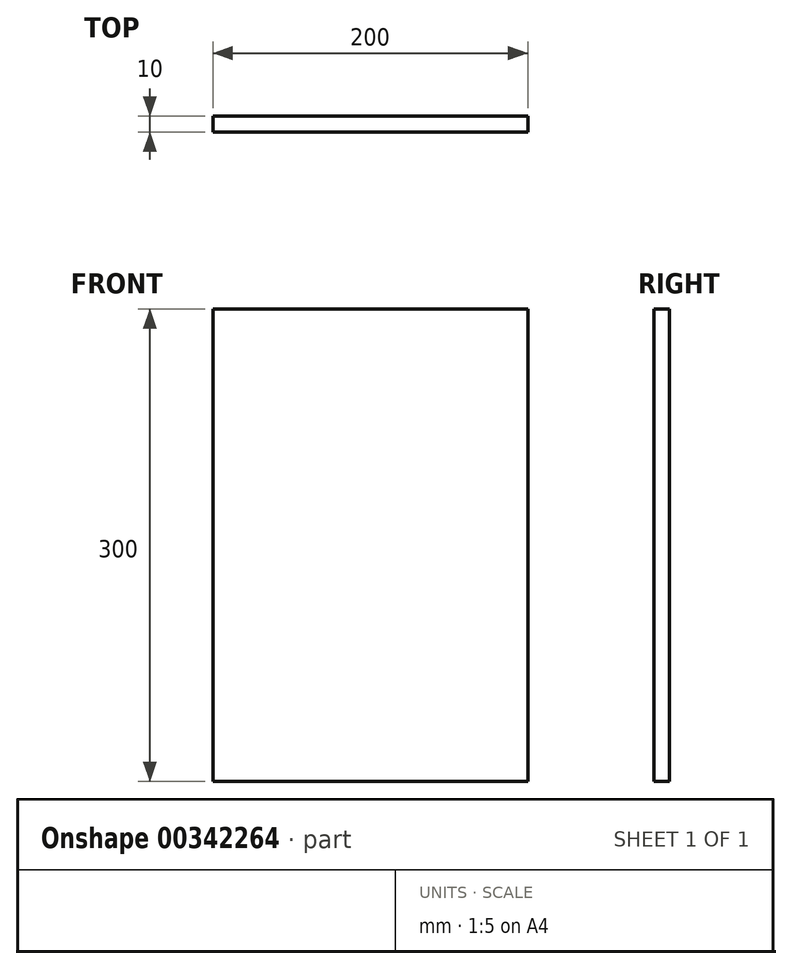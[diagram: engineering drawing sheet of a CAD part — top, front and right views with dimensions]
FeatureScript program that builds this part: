
annotation { "Feature Type Name" : "Feature", "Feature Type Description" : "" }
export const myFeature = defineFeature(function(context is Context, id is Id, definition is map)
    precondition{}
    {
        {
            var Q0;
            Q0=qCreatedBy(makeId("Front.planeOp"),FACE);
            var sketch = newSketch(context, id + "F0", { "sketchPlane" : qUnion([Q0])});
            skLineSegment(sketch, "E0.bottom", {"start": v(-134.06, 174.62) * mm, "end": v(65.94, 174.62) * mm});
            skLineSegment(sketch, "E0.top", {"start": v(-134.06, -125.38) * mm, "end": v(65.94, -125.38) * mm});
            skLineSegment(sketch, "E0.left", {"start": v(-134.06, 174.62) * mm, "end": v(-134.06, -125.38) * mm});
            skLineSegment(sketch, "E0.right", {"start": v(65.94, 174.62) * mm, "end": v(65.94, -125.38) * mm});
            skSolve(sketch);
        }
        {
            var Q0;
            Q0=makeQuery(id+"F0.imprint","IMPRINT",FACE,{"disambiguationData":[TD([[makeQuery(id+"F0.imprint","IMPRINT",EDGE,{"derivedFrom":sQuery(id+"F0.wireOp",EDGE,"E0.bottom")}),-1.0]])]});
            extrude(context, id + "F1", {"entities" : qUnion([Q0]), "depth" : 10 * mm});
        }
    });
